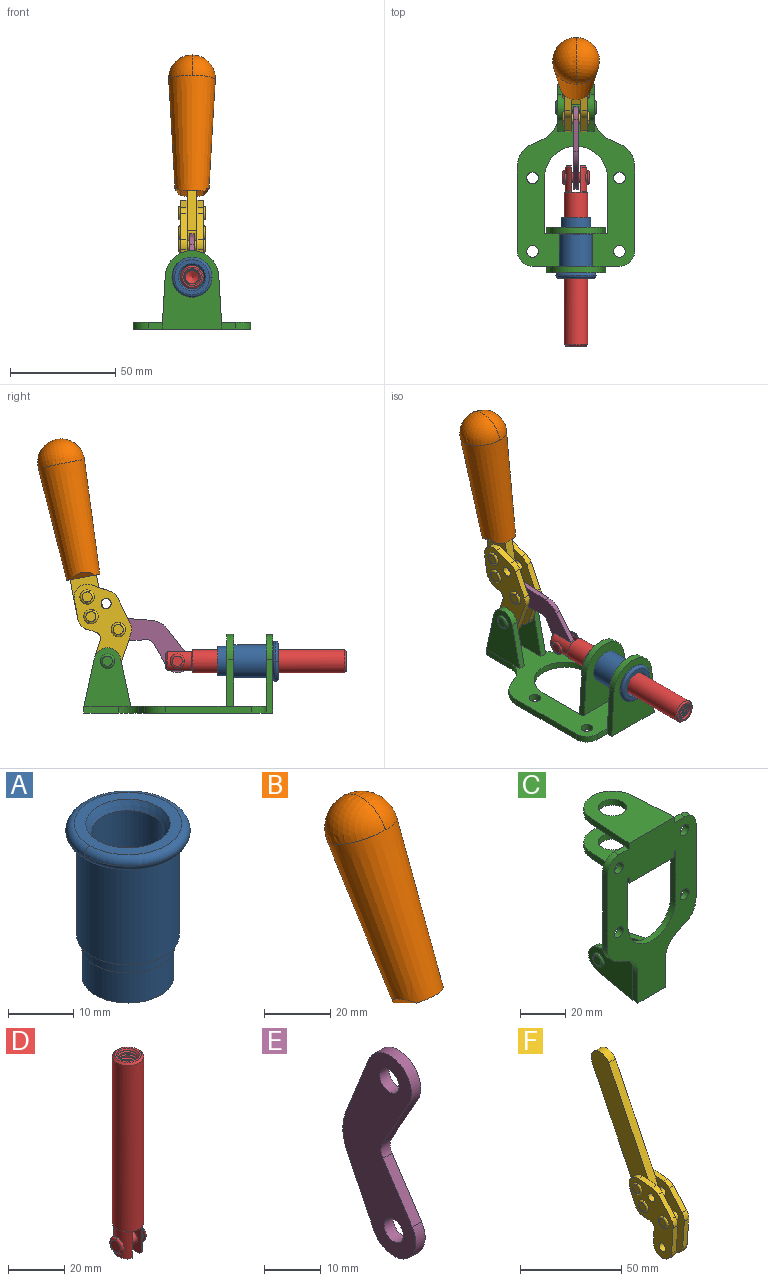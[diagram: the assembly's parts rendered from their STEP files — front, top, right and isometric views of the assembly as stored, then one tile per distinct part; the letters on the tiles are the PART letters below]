
ASSEMBLY  parts=6 mates=6
PART A: 15 faces, bbox 20.6x20.6x28.7 mm
  f0: torus R=8.26mm, axis (0,0,1), area 56.8mm2, adj f1,f10,f12
  f1: torus R=8.26mm, axis (0,0,1), area 56.8mm2, adj f0,f6,f13
  f2: cylinder r=5.59mm len=25.91mm, axis (0,0,1), area 909.6mm2, adj f3,f4
  f3: cone r=6.86mm half-angle=45deg, axis (0,0,-1), area 70.2mm2, adj f2,f14
  f4: cone r=6.47mm half-angle=30deg, axis (0,0,1), area 66.7mm2, adj f2,f13
  f5: cylinder r=7.04mm len=14.07mm, axis (0,0,1), area 252.6mm2, adj f11,f14
  f6: torus R=8.26mm, axis (0,0,1), area 56.8mm2, adj f1,f12,f13
  f7: cylinder r=7.16mm len=14.33mm, axis (0,0,1), area 91.5mm2, adj f9,f11
  f8: cylinder r=7.86mm len=18.42mm, axis (0,0,1), area 909.6mm2, adj f9,f10
  f9: plane 15.72x15.72mm, normal (0,0,-1), area 33mm2, adj f7,f8
  f10: plane 16.51x16.51mm, normal (0,0,-1), area 19.9mm2, adj f0,f8,f12
  f11: plane 14.33x14.33mm, normal (0,0,-1), area 5.7mm2, adj f5,f7
  f12: torus R=8.26mm, axis (0,0,1), area 56.8mm2, adj f0,f6,f10
  f13: plane 16.51x16.51mm, normal (0,0,1), area 82.7mm2, adj f1,f4,f6
  f14: plane 14.07x14.07mm, normal (0,0,-1), area 7.8mm2, adj f3,f5
PART B: 11 faces, bbox 22.3x42.6x64.5 mm
  f0: sphere r=11.13mm, area 411.4mm2, adj f1,f8
  f1: cone r=11.11mm half-angle=3.3deg, axis (0,0.44,0.9), area 3251.8mm2, adj f0,f7,f8,f9,f10
  f2: cylinder r=6.16mm len=11.7mm, axis (1,0,0), area 89.5mm2, adj f3,f4,f5,f6
  f3: plane 60.23x36.75mm, normal (-1,0,0), area 763.6mm2, adj f2,f4,f6,f10
  f4: plane 51.37x25.05mm, normal (0,0.9,-0.44), area 264.2mm2, adj f2,f3,f5,f10
  f5: plane 60.23x36.75mm, normal (1,0,0), area 763.6mm2, adj f2,f4,f6,f10
  f6: plane 51.37x25.05mm, normal (0,-0.9,0.44), area 264.2mm2, adj f2,f3,f5,f10
  f7: plane 9.95x5.95mm, normal (0.71,-0.31,-0.64), area 25.8mm2, adj f1,f10
  f8: sphere r=11.13mm, area 411.4mm2, adj f0,f1
  f9: plane 9.95x5.95mm, normal (-0.71,-0.31,-0.64), area 25.8mm2, adj f1,f10
  f10: plane 14.27x11.38mm, normal (0,-0.44,-0.9), area 106.7mm2, adj f1,f3,f4,f5,f6,f7,f9
PART C: 55 faces, bbox 55.7x37.4x89.8 mm
  f0: torus R=2.41mm, axis (-1,0,0), area 15mm2, adj f11,f15,f25
  f1: torus R=2.41mm, axis (-1,0,0), area 15mm2, adj f10,f12,f22
  f2: cylinder r=2.78mm len=5.56mm, axis (0,-1,0), area 54.2mm2, adj f30,f54
  f3: cylinder r=14.99mm len=29.97mm, axis (0,-1,0), area 145.9mm2, adj f30,f49,f53,f54
  f4: cylinder r=2.78mm len=5.56mm, axis (0,-1,0), area 54.2mm2, adj f30,f54
  f5: cylinder r=2.78mm len=5.56mm, axis (0,-1,0), area 54.2mm2, adj f30,f54
  f6: cylinder r=2.78mm len=5.56mm, axis (0,-1,0), area 54.2mm2, adj f30,f54
  f7: cylinder r=6.35mm len=12.7mm, axis (0,0,1), area 123.6mm2, adj f27,f51
  f8: cylinder r=6.35mm len=12.7mm, axis (0,0,-1), area 124.7mm2, adj f21,f35
  f9: cylinder r=2.41mm len=11.18mm, axis (-1,0,0), area 169.4mm2, adj f16,f19
  f10: plane 4.83x4.83mm, normal (1,0,0), area 18.3mm2, adj f1,f12
  f11: plane 4.83x4.83mm, normal (-1,0,0), area 18.3mm2, adj f0,f15
  f12: torus R=2.41mm, axis (-1,0,0), area 15mm2, adj f1,f10,f22
  f13: cylinder r=6.35mm len=12.41mm, axis (1,0,0), area 53.4mm2, adj f18,f19,f22,f23
  f14: cylinder r=6.35mm len=12.41mm, axis (-1,0,0), area 53.4mm2, adj f16,f17,f24,f25
  f15: torus R=2.41mm, axis (-1,0,0), area 15mm2, adj f0,f11,f25
  f16: plane 27.86x22.35mm, normal (1,0,0), area 425.4mm2, adj f9,f14,f17,f24,f30
  f17: plane 22.86x4.97mm, normal (0,0.21,0.98), area 72.5mm2, adj f14,f16,f25,f30
  f18: plane 22.86x4.97mm, normal (0,0.21,0.98), area 72.5mm2, adj f13,f19,f22,f30
  f19: plane 27.86x22.35mm, normal (-1,0,0), area 425.4mm2, adj f9,f13,f18,f23,f30
  f20: cylinder r=12.7mm len=25.35mm, axis (0,0,-1), area 119.8mm2, adj f21,f34,f35,f36
  f21: plane 34.21x28.07mm, normal (0,0,-1), area 702.4mm2, adj f8,f20,f30,f34,f36
  f22: plane 27.96x22.45mm, normal (1,0,0), area 407.2mm2, adj f1,f12,f13,f18,f23,f30,f42,f43
  f23: plane 22.86x4.97mm, normal (0,0.21,-0.98), area 72.5mm2, adj f13,f19,f22,f44
  f24: plane 22.86x4.97mm, normal (0,0.21,-0.98), area 72.5mm2, adj f14,f16,f25,f44
  f25: plane 27.86x22.35mm, normal (-1,0,0), area 407.1mm2, adj f0,f14,f15,f17,f24,f30,f45,f46
  f26: plane 3.1x0.95mm, normal (0,0,-1), area 2.7mm2, adj f30,f49,f50,f54
  f27: plane 34.21x28.07mm, normal (0,0,1), area 702.4mm2, adj f7,f28,f30,f50,f52
  f28: cylinder r=12.7mm len=25.35mm, axis (0,0,1), area 118.8mm2, adj f27,f50,f51,f52
  f29: plane 3.1x0.95mm, normal (0,0,-1), area 2.7mm2, adj f30,f52,f53,f54
  f30: plane 86.54x55.63mm, normal (0,1,0), area 2362.9mm2, adj f2,f3,f4,f5,f6,f16,f17,f18
  f31: plane 40.56x3.1mm, normal (-1,0,0), area 125.7mm2, adj f30,f32,f48,f54
  f32: cylinder r=7.11mm len=7.11mm, axis (0,-1,0), area 34.6mm2, adj f30,f31,f33,f54
  f33: plane 6.67x3.1mm, normal (0,0,1), area 20.4mm2, adj f30,f32,f34,f54
  f34: plane 25.39x3.13mm, normal (-1,0.06,0), area 79.5mm2, adj f20,f21,f33,f35,f54
  f35: plane 37.31x28.45mm, normal (0,0,1), area 789.9mm2, adj f8,f20,f34,f36,f54
  f36: plane 25.39x3.13mm, normal (1,0.06,0), area 79.5mm2, adj f20,f21,f35,f37,f54
  f37: plane 6.67x3.1mm, normal (0,0,1), area 20.4mm2, adj f30,f36,f38,f54
  f38: cylinder r=7.11mm len=7.11mm, axis (0,-1,0), area 34.6mm2, adj f30,f37,f39,f54
  f39: plane 40.56x3.1mm, normal (1,0,0), area 125.7mm2, adj f30,f38,f40,f54
  f40: cylinder r=11.18mm len=10.16mm, axis (0,-1,0), area 39.5mm2, adj f30,f39,f41,f54
  f41: plane 6.09x3.1mm, normal (0.42,0,-0.91), area 20.8mm2, adj f30,f40,f42,f54
  f42: cylinder r=11.18mm len=9.41mm, axis (0,-1,0), area 37.2mm2, adj f22,f30,f41,f43,f54
  f43: plane 16.5x3.1mm, normal (1,0,0), area 51.1mm2, adj f22,f42,f44,f54
  f44: plane 17.37x3.1mm, normal (0,0,-1), area 53.8mm2, adj f23,f24,f30,f43,f45,f54
  f45: plane 16.5x3.1mm, normal (-1,0,0), area 51.1mm2, adj f25,f44,f46,f54
  f46: cylinder r=11.18mm len=9.41mm, axis (0,-1,0), area 37.2mm2, adj f25,f30,f45,f47,f54
  f47: plane 6.09x3.1mm, normal (-0.42,0,-0.91), area 20.8mm2, adj f30,f46,f48,f54
  f48: cylinder r=11.18mm len=10.16mm, axis (0,-1,0), area 39.5mm2, adj f30,f31,f47,f54
  f49: plane 26.54x3.1mm, normal (-1,0,0), area 82.3mm2, adj f3,f26,f30,f54
  f50: plane 25.39x3.1mm, normal (1,0.06,0), area 78.8mm2, adj f26,f27,f28,f51,f54
  f51: plane 37.31x28.45mm, normal (0,0,-1), area 789.9mm2, adj f7,f28,f50,f52,f54
  f52: plane 25.39x3.1mm, normal (-1,0.06,0), area 78.8mm2, adj f27,f28,f29,f51,f54
  f53: plane 26.54x3.1mm, normal (1,0,0), area 82.3mm2, adj f3,f29,f30,f54
  f54: plane 89.66x55.63mm, normal (0,-1,0), area 2678.5mm2, adj f2,f3,f4,f5,f6,f26,f29,f31
PART D: 48 faces, bbox 12.6x11.1x86.1 mm
  f0: torus R=2.41mm, axis (-1,0,0), area 15mm2, adj f30,f32,f34
  f1: torus R=2.41mm, axis (-1,0,0), area 15mm2, adj f29,f31,f33
  f2: cylinder r=5.54mm len=72.39mm, axis (0,0,1), area 2518.5mm2, adj f3,f4,f42,f43
  f3: cone r=5.54mm half-angle=45deg, axis (0,0,1), area 7.6mm2, adj f2,f5,f41
  f4: cone r=5.54mm half-angle=45deg, axis (0,0,-1), area 34.9mm2, adj f2,f39
  f5: cylinder r=5.08mm len=11.48mm, axis (0,0,1), area 108.3mm2, adj f3,f7,f8,f41
  f6: cylinder r=2.41mm len=4.83mm, axis (-1,0,0), area 71.2mm2, adj f40,f41
  f7: cylinder r=2.41mm len=4.83mm, axis (-1,0,0), area 7.6mm2, adj f5,f34
  f8: cone r=5.08mm half-angle=45deg, axis (0,0,1), area 10.6mm2, adj f5,f37,f41
  f9: cone r=3.98mm half-angle=45deg, axis (0,0,1), area 17.6mm2, adj f27,f39,f45,f46,f47
  f10: cylinder r=2.41mm len=4.83mm, axis (-1,0,0), area 7.6mm2, adj f33,f38
  f11: cylinder r=3.2mm len=6.4mm, axis (0,0,1), area 78.4mm2, adj f12,f28,f44,f45,f47
  f12: cylinder r=3.2mm len=6.4mm, axis (0,0,1), area 10.5mm2, adj f11,f13,f45,f47
  f13: cylinder r=3.2mm len=6.4mm, axis (0,0,1), area 10.5mm2, adj f12,f14,f45,f47
  f14: cylinder r=3.2mm len=6.4mm, axis (0,0,1), area 10.5mm2, adj f13,f15,f45,f47
  f15: cylinder r=3.2mm len=6.4mm, axis (0,0,1), area 10.5mm2, adj f14,f16,f45,f47
  f16: cylinder r=3.2mm len=6.4mm, axis (0,0,1), area 10.5mm2, adj f15,f17,f45,f47
  f17: cylinder r=3.2mm len=6.4mm, axis (0,0,1), area 10.5mm2, adj f16,f18,f45,f47
  f18: cylinder r=3.2mm len=6.4mm, axis (0,0,1), area 10.5mm2, adj f17,f19,f45,f47
  f19: cylinder r=3.2mm len=6.4mm, axis (0,0,1), area 10.5mm2, adj f18,f20,f45,f47
  f20: cylinder r=3.2mm len=6.4mm, axis (0,0,1), area 10.5mm2, adj f19,f21,f45,f47
  f21: cylinder r=3.2mm len=6.4mm, axis (0,0,1), area 10.5mm2, adj f20,f22,f45,f47
  f22: cylinder r=3.2mm len=6.4mm, axis (0,0,1), area 10.5mm2, adj f21,f23,f45,f47
  f23: cylinder r=3.2mm len=6.4mm, axis (0,0,1), area 10.5mm2, adj f22,f24,f45,f47
  f24: cylinder r=3.2mm len=6.4mm, axis (0,0,1), area 10.5mm2, adj f23,f25,f45,f47
  f25: cylinder r=3.2mm len=6.4mm, axis (0,0,1), area 10.5mm2, adj f24,f26,f45,f47
  f26: cylinder r=3.2mm len=6.4mm, axis (0,0,1), area 10.5mm2, adj f25,f27,f45,f47
  f27: cylinder r=3.2mm len=6.4mm, axis (0,0,1), area 7.4mm2, adj f9,f26,f45,f47
  f28: cone r=3.2mm half-angle=60deg, axis (0,0,1), area 37.2mm2, adj f11
  f29: plane 4.83x4.83mm, normal (-1,0,0), area 18.3mm2, adj f1,f31
  f30: plane 4.83x4.83mm, normal (1,0,0), area 18.3mm2, adj f0,f32
  f31: torus R=2.41mm, axis (-1,0,0), area 15mm2, adj f1,f29,f33
  f32: torus R=2.41mm, axis (-1,0,0), area 15mm2, adj f0,f30,f34
  f33: plane 6.83x6.83mm, normal (1,0,0), area 18.3mm2, adj f1,f10,f31
  f34: plane 6.83x6.83mm, normal (-1,0,0), area 18.3mm2, adj f0,f7,f32
  f35: cone r=5.08mm half-angle=45deg, axis (0,0,1), area 10.6mm2, adj f36,f38,f40
  f36: plane 7.25x1.97mm, normal (0,0,-1), area 10mm2, adj f35,f40
  f37: plane 7.25x1.97mm, normal (0,0,-1), area 10mm2, adj f8,f41
  f38: cylinder r=5.08mm len=11.48mm, axis (0,0,1), area 108.3mm2, adj f10,f35,f40,f42
  f39: plane 9.55x9.55mm, normal (0,0,1), area 22mm2, adj f4,f9
  f40: plane 12.76x10.09mm, normal (1,0,0), area 95.7mm2, adj f6,f35,f36,f38,f42,f43
  f41: plane 12.76x10.09mm, normal (-1,0,0), area 95.7mm2, adj f3,f5,f6,f8,f37,f43
  f42: cone r=5.54mm half-angle=45deg, axis (0,0,1), area 7.6mm2, adj f2,f38,f40
  f43: plane 11.07x4.7mm, normal (0,0,-1), area 50.4mm2, adj f2,f40,f41
  f44: plane 0.89x0.62mm, normal (-1,0,0), area 0.3mm2, adj f11,f45,f46,f47
  f45: bspline ~24.8x7.63mm, area 266.6mm2, adj f9,f11,f12,f13,f14,f15,f16,f17
  f46: bspline ~24.87x7.63mm, area 73.6mm2, adj f9,f44,f45,f47
  f47: bspline ~24.98x7.63mm, area 272.5mm2, adj f9,f11,f12,f13,f14,f15,f16,f17
PART E: 12 faces, bbox 2.3x18.2x42.8 mm
  f0: cylinder r=2.4mm len=4.8mm, axis (1,0,0), area 34.9mm2, adj f4,f11
  f1: cylinder r=10.41mm len=8.47mm, axis (1,0,0), area 20.2mm2, adj f4,f9,f10,f11
  f2: cylinder r=3.05mm len=3.16mm, axis (1,0,0), area 7.7mm2, adj f4,f6,f7,f11
  f3: cylinder r=2.4mm len=4.8mm, axis (1,0,0), area 34.9mm2, adj f4,f11
  f4: plane 42.81x18.23mm, normal (-1,0,0), area 414.1mm2, adj f0,f1,f2,f3,f5,f6,f7,f8
  f5: cylinder r=5.54mm len=10.67mm, axis (1,0,0), area 41.8mm2, adj f4,f6,f10,f11
  f6: plane 11.66x6.53mm, normal (0,-0.87,-0.49), area 30.9mm2, adj f2,f4,f5,f11
  f7: plane 11.17x7.33mm, normal (0,-0.84,0.55), area 30.9mm2, adj f2,f4,f8,f11
  f8: cylinder r=5.54mm len=10.51mm, axis (1,0,0), area 41.8mm2, adj f4,f7,f9,f11
  f9: plane 13.67x6.67mm, normal (0,0.9,-0.44), area 35.1mm2, adj f1,f4,f8,f11
  f10: plane 14.1x5.7mm, normal (0,0.93,0.37), area 35.1mm2, adj f1,f4,f5,f11
  f11: plane 42.81x18.23mm, normal (1,0,0), area 414.1mm2, adj f0,f1,f2,f3,f5,f6,f7,f8
PART F: 59 faces, bbox 12.9x60.2x99.6 mm
  f0: torus R=2.39mm, axis (-1,0,0), area 14.9mm2, adj f20,f43,f51
  f1: torus R=2.39mm, axis (-1,0,0), area 14.9mm2, adj f19,f42,f51
  f2: torus R=2.39mm, axis (-1,0,0), area 14.9mm2, adj f18,f35,f51
  f3: torus R=2.39mm, axis (-1,0,0), area 14.9mm2, adj f14,f17,f23
  f4: torus R=2.39mm, axis (-1,0,0), area 14.9mm2, adj f13,f16,f23
  f5: torus R=2.39mm, axis (-1,0,0), area 14.9mm2, adj f12,f15,f23
  f6: cylinder r=2.39mm len=4.78mm, axis (1,0,0), area 46.5mm2, adj f48,f50,f51
  f7: cylinder r=2.39mm len=4.78mm, axis (1,0,0), area 46.5mm2, adj f50,f51
  f8: cylinder r=6.35mm len=12.68mm, axis (1,0,0), area 61.8mm2, adj f38,f39,f50,f51
  f9: cylinder r=2.39mm len=4.78mm, axis (-1,0,0), area 70.5mm2, adj f46,f50
  f10: cylinder r=2.39mm len=4.78mm, axis (-1,0,0), area 46.5mm2, adj f23,f45,f46
  f11: cylinder r=2.39mm len=4.78mm, axis (-1,0,0), area 46.5mm2, adj f23,f46
  f12: plane 4.78x4.78mm, normal (1,0,0), area 17.9mm2, adj f5,f15
  f13: plane 4.78x4.78mm, normal (1,0,0), area 17.9mm2, adj f4,f16
  f14: plane 4.78x4.78mm, normal (1,0,0), area 17.9mm2, adj f3,f17
  f15: torus R=2.39mm, axis (-1,0,0), area 14.9mm2, adj f5,f12,f23
  f16: torus R=2.39mm, axis (-1,0,0), area 14.9mm2, adj f4,f13,f23
  f17: torus R=2.39mm, axis (-1,0,0), area 14.9mm2, adj f3,f14,f23
  f18: plane 4.78x4.78mm, normal (-1,0,0), area 17.9mm2, adj f2,f35
  f19: plane 4.78x4.78mm, normal (-1,0,0), area 17.9mm2, adj f1,f42
  f20: plane 4.78x4.78mm, normal (-1,0,0), area 17.9mm2, adj f0,f43
  f21: plane 2.26x0.2mm, normal (1,0,0), area 0.2mm2, adj f31,f44
  f22: plane 2.26x0.2mm, normal (-1,0,0), area 0.2mm2, adj f41,f44
  f23: plane 39.37x30.77mm, normal (1,0,0), area 565.5mm2, adj f3,f4,f5,f10,f11,f15,f16,f17
  f24: cylinder r=6.1mm len=4.15mm, axis (-1,0,0), area 14.7mm2, adj f23,f25,f32,f46
  f25: plane 10.25x9.01mm, normal (0,-0.75,0.66), area 42.3mm2, adj f23,f24,f26,f46
  f26: cylinder r=6.35mm len=4.64mm, axis (-1,0,0), area 15.6mm2, adj f23,f25,f27,f46
  f27: plane 15.84x3.1mm, normal (0,-1,-0.07), area 49.2mm2, adj f23,f26,f28,f46
  f28: cylinder r=6.35mm len=12.68mm, axis (-1,0,0), area 61.8mm2, adj f23,f27,f29,f46
  f29: plane 8.11x3.1mm, normal (0,1,0.07), area 25.2mm2, adj f23,f28,f30,f46
  f30: cylinder r=3.05mm len=3.25mm, axis (-1,0,0), area 14.8mm2, adj f23,f29,f31,f46
  f31: plane 5.99x3.1mm, normal (0,0.07,-1), area 18.6mm2, adj f21,f23,f30,f44,f46
  f32: plane 9.5x3.1mm, normal (0,-0.07,1), area 29.5mm2, adj f23,f24,f33,f46,f47
  f33: cylinder r=6.1mm len=8.63mm, axis (-1,0,0), area 39.1mm2, adj f23,f32,f34,f47
  f34: plane 8.65x3.96mm, normal (0,0.91,-0.42), area 29.5mm2, adj f23,f33,f44,f47
  f35: torus R=2.39mm, axis (-1,0,0), area 14.9mm2, adj f2,f18,f51
  f36: plane 10.25x9.01mm, normal (0,-0.75,0.66), area 42.3mm2, adj f37,f49,f50,f51
  f37: cylinder r=6.35mm len=4.64mm, axis (1,0,0), area 15.6mm2, adj f36,f38,f50,f51
  f38: plane 15.84x3.1mm, normal (0,-1,-0.07), area 49.2mm2, adj f8,f37,f50,f51
  f39: plane 8.11x3.1mm, normal (0,1,0.07), area 25.2mm2, adj f8,f40,f50,f51
  f40: cylinder r=3.05mm len=3.25mm, axis (1,0,0), area 14.8mm2, adj f39,f41,f50,f51
  f41: plane 5.99x3.1mm, normal (0,0.07,-1), area 18.6mm2, adj f22,f40,f44,f50,f51
  f42: torus R=2.39mm, axis (-1,0,0), area 14.9mm2, adj f1,f19,f51
  f43: torus R=2.39mm, axis (-1,0,0), area 14.9mm2, adj f0,f20,f51
  f44: cylinder r=6.35mm len=12.12mm, axis (-1,0,0), area 128.9mm2, adj f21,f22,f23,f31,f34,f41,f46,f47
  f45: plane 2.65x1.35mm, normal (1,0,0), area 1mm2, adj f10,f55
  f46: plane 39.08x20.42mm, normal (-1,0,0), area 412.5mm2, adj f9,f10,f11,f24,f25,f26,f27,f28
  f47: plane 77.62x39.82mm, normal (1,0,0), area 850mm2, adj f32,f33,f34,f44,f53,f54,f55
  f48: plane 2.65x1.35mm, normal (-1,0,0), area 1mm2, adj f6,f55
  f49: cylinder r=6.1mm len=4.15mm, axis (1,0,0), area 14.7mm2, adj f36,f50,f51,f56
  f50: plane 39.08x20.42mm, normal (1,0,0), area 412.5mm2, adj f6,f7,f8,f9,f36,f37,f38,f39
  f51: plane 39.37x30.77mm, normal (-1,0,0), area 565.5mm2, adj f0,f1,f2,f6,f7,f8,f35,f36
  f52: plane 8.65x3.96mm, normal (0,0.91,-0.42), area 29.5mm2, adj f44,f51,f57,f58
  f53: plane 68.49x33.4mm, normal (0,0.9,-0.44), area 358.1mm2, adj f44,f47,f54,f58
  f54: cylinder r=6.35mm len=12.06mm, axis (1,0,0), area 93.7mm2, adj f47,f53,f55,f58
  f55: plane 68.49x33.4mm, normal (0,-0.9,0.44), area 358.1mm2, adj f44,f45,f46,f47,f48,f50,f54,f58
  f56: plane 9.5x3.1mm, normal (0,-0.07,1), area 29.5mm2, adj f49,f50,f51,f57,f58
  f57: cylinder r=6.1mm len=8.63mm, axis (1,0,0), area 39.1mm2, adj f51,f52,f56,f58
  f58: plane 77.62x39.82mm, normal (-1,0,0), area 850mm2, adj f44,f52,f53,f54,f55,f56,f57
PLACE A rot(axis=(1,0,0),90deg) t=(0,9.14,0)mm
PLACE B rot(axis=(1,0,0),15deg) t=(0,9.13,49.22)mm
PLACE C rot(axis=(1,0,0),90deg) t=(0,9.14,0)mm fixed
PLACE D rot(axis=(1,0,0),90deg) t=(0,23.55,0)mm
PLACE E rot(axis=(1,0,0),120.2deg) t=(0,33.83,11.13)mm
PLACE F rot(axis=(1,0,0),15deg) t=(0,9.13,49.22)mm
MATE revolute E.f5 <-> D.f6  axis (1,0,0) through (0,8.07,24.61)mm
MATE fastened B.f2 <-> F.f54  axis (1,0,0) through (0,63.52,120.55)mm
MATE fastened A.f0 <-> C.f7  axis (0,1,0) through (0,-37.25,24.61)mm
MATE revolute E.f3 <-> F.f4  axis (1,0,0) through (0,36.05,39.62)mm
MATE revolute C.f0 <-> F.f7  axis (-1,0,0) through (0,41.23,24.61)mm
MATE slider D.f2 <-> C.f7  axis (0,-1,0) through (0,-35.23,24.61)mm
